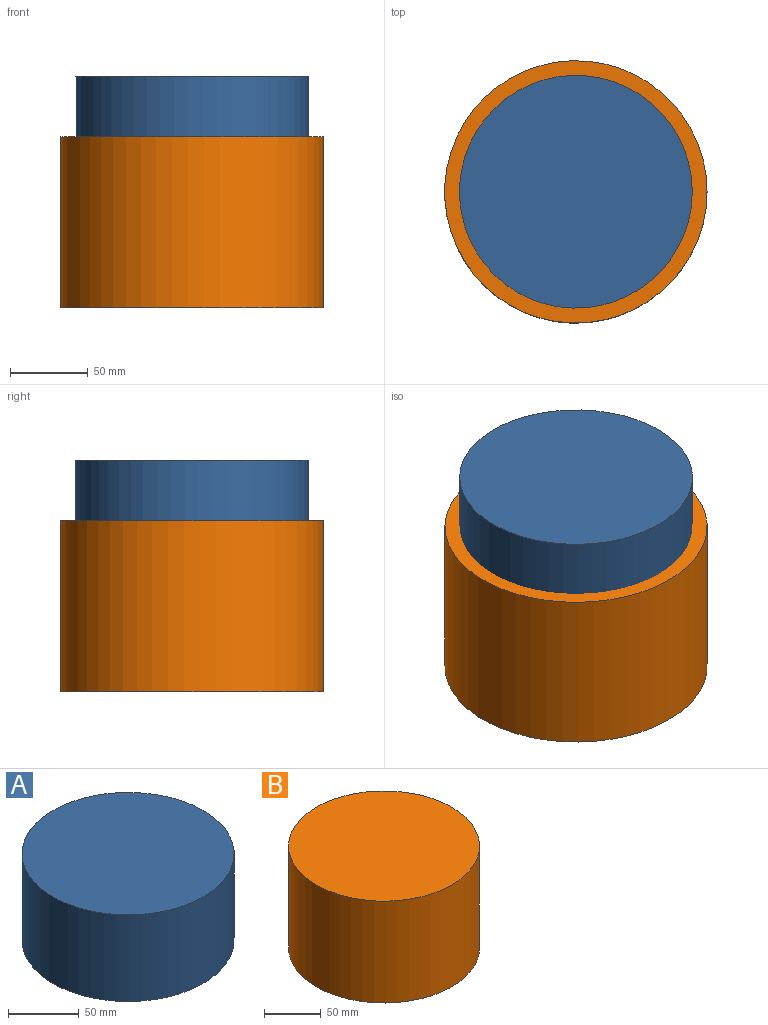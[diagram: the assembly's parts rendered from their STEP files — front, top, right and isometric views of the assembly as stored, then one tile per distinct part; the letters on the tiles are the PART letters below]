
ASSEMBLY  parts=2 mates=1
PART A: 3 faces, bbox 150x150x75 mm
  f0: cylinder r=75mm len=150mm, axis (0,0,-1), area 35342.9mm2, adj f1,f2
  f1: plane 150x150mm, normal (0,0,1), area 17671.5mm2, adj f0
  f2: plane 150x150mm, normal (0,0,-1), area 17671.5mm2, adj f0
PART B: 3 faces, bbox 169x169x110.3 mm
  f0: cylinder r=84.5mm len=169mm, axis (0,0,-1), area 58534.9mm2, adj f1,f2
  f1: plane 169x169mm, normal (0,0,1), area 22431.8mm2, adj f0
  f2: plane 169x169mm, normal (0,0,-1), area 22431.8mm2, adj f0
PLACE A rot(axis=(1,0,0),180deg) t=(0,0,149.3)mm
PLACE B rot(axis=(1,0,0),180deg) t=(0,0,110.25)mm
MATE fastened A.f0 <-> B.f0  axis (0,0,-1) through (0,0,74.3)mm
